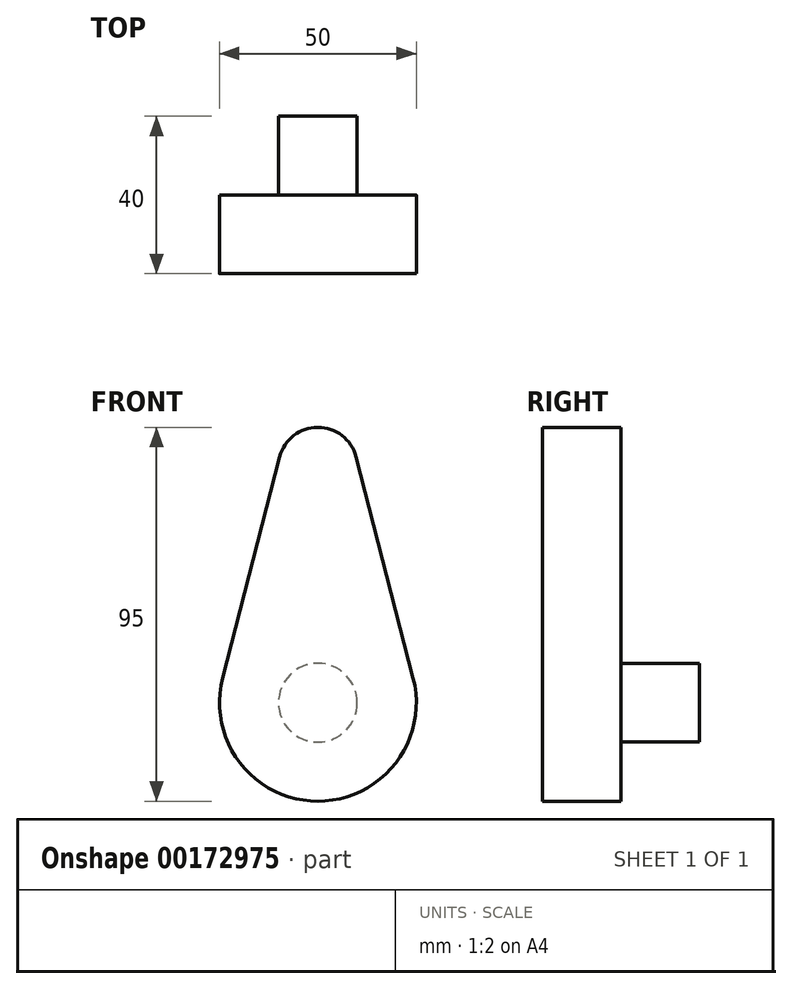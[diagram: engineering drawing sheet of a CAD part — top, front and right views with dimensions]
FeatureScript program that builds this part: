
annotation { "Feature Type Name" : "Feature", "Feature Type Description" : "" }
export const myFeature = defineFeature(function(context is Context, id is Id, definition is map)
    precondition{}
    {
        {
            var Q0;
            Q0=qCreatedBy(makeId("Front.planeOp"),FACE);
            var sketch = newSketch(context, id + "F0", { "sketchPlane" : qUnion([Q0])});
            skCircle(sketch, "E0", {"center": v(0, 0) * mm, "radius": 25 * mm});
            skCircle(sketch, "E1", {"center": v(0, 60) * mm, "radius": 10 * mm});
            skLineSegment(sketch, "E2", {"start": v(0, 60) * mm, "end": v(0, 0) * mm, "construction": true});
            skLineSegment(sketch, "E3", {"start": v(-24.2, 6.25) * mm, "end": v(-9.68, 62.5) * mm});
            skLineSegment(sketch, "E4.MirrorCS", {"start": v(24.2, 6.25) * mm, "end": v(9.68, 62.5) * mm});
            skSolve(sketch);
        }
        {
            var Q0;
            {var subQ0=sQuery(id+"F0.wireOp",EDGE,"E3");Q0=makeQuery(id+"F0.imprint","IMPRINT",FACE,{"disambiguationData":[TD([[makeQuery(id+"F0.imprint","IMPRINT",EDGE,{"derivedFrom":subQ0}),-1.0]])]});}
            var Q1;
            {var subQ0=sQuery(id+"F0.wireOp",EDGE,"E0");var subQ1=makeQuery(id+"F0.imprint","INTERSECT",VERTEX,{"derivedFrom":[subQ0,sQuery(id+"F0.wireOp",EDGE,"E3")]});Q1=makeQuery(id+"F0.imprint","IMPRINT",FACE,{"disambiguationData":[TD([[makeQuery(id+"F0.imprint","IMPRINT",EDGE,{"disambiguationData":[TD([[subQ1,1.0]])],"derivedFrom":subQ0}),1.0]])]});}
            var Q2;
            {var subQ0=sQuery(id+"F0.wireOp",EDGE,"E1");var subQ1=makeQuery(id+"F0.imprint","INTERSECT",VERTEX,{"derivedFrom":[subQ0,sQuery(id+"F0.wireOp",EDGE,"E3")]});Q2=makeQuery(id+"F0.imprint","IMPRINT",FACE,{"disambiguationData":[TD([[makeQuery(id+"F0.imprint","IMPRINT",EDGE,{"disambiguationData":[TD([[subQ1,1.0]])],"derivedFrom":subQ0}),1.0]])]});}
            extrude(context, id + "F1", {"entities" : qUnion([Q0, Q1, Q2]), "depth" : 20 * mm});
        }
        {
            var Q0;
            Q0=makeQuery(id+"F1.opExtrude","CAP_FACE",FACE,{"disambiguationData":[OSD([sQuery(id+"F0.wireOp",EDGE,"E0"),sQuery(id+"F0.wireOp",EDGE,"E1"),sQuery(id+"F0.wireOp",EDGE,"E3"),sQuery(id+"F0.wireOp",EDGE,"E4.MirrorCS")])],"isStart":true});
            var sketch = newSketch(context, id + "F2", { "sketchPlane" : qUnion([Q0])});
            skCircle(sketch, "E5", {"center": v(0, 0) * mm, "radius": 10 * mm});
            skSolve(sketch);
        }
        {
            var Q0;
            Q0 = qSketchRegion(id + "F2", true);
            extrude(context, id + "F3", {"entities" : qUnion([Q0]), "operationType" : NewBodyOperationType.ADD, "depth" : 20 * mm});
        }
    });
